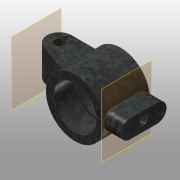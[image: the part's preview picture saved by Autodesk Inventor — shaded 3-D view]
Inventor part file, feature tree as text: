
AUTODESK INVENTOR PART (.ipt)
format: ipt  version: 2015 (Build 190159000, 159)  size: 174,592 bytes
history: native  units: mm
features: sketch x8, other x3, plane x2
ambient origin geometry x8: Origin, YZ Plane, XZ Plane, XY Plane, X Axis, Y Axis, Z Axis, Center Point
bodies: Solid1 (feature_tree)
feature tree (13):
  other  "500-007.ipt"
  other  "Solid1::500-007.ipt"
  other  "TaggingFeature1"
  sketch  "Sketch1"  dims[d0=10.0mm]
  sketch  "Sketch2"
  sketch  "Sketch3"
  sketch  "Sketch5"
  sketch  "Sketch6"
  sketch  "Sketch7"
  sketch  "Sketch8"
  sketch  "Sketch9"
  plane  "Work Plane1"
  plane  "Work Plane2"
